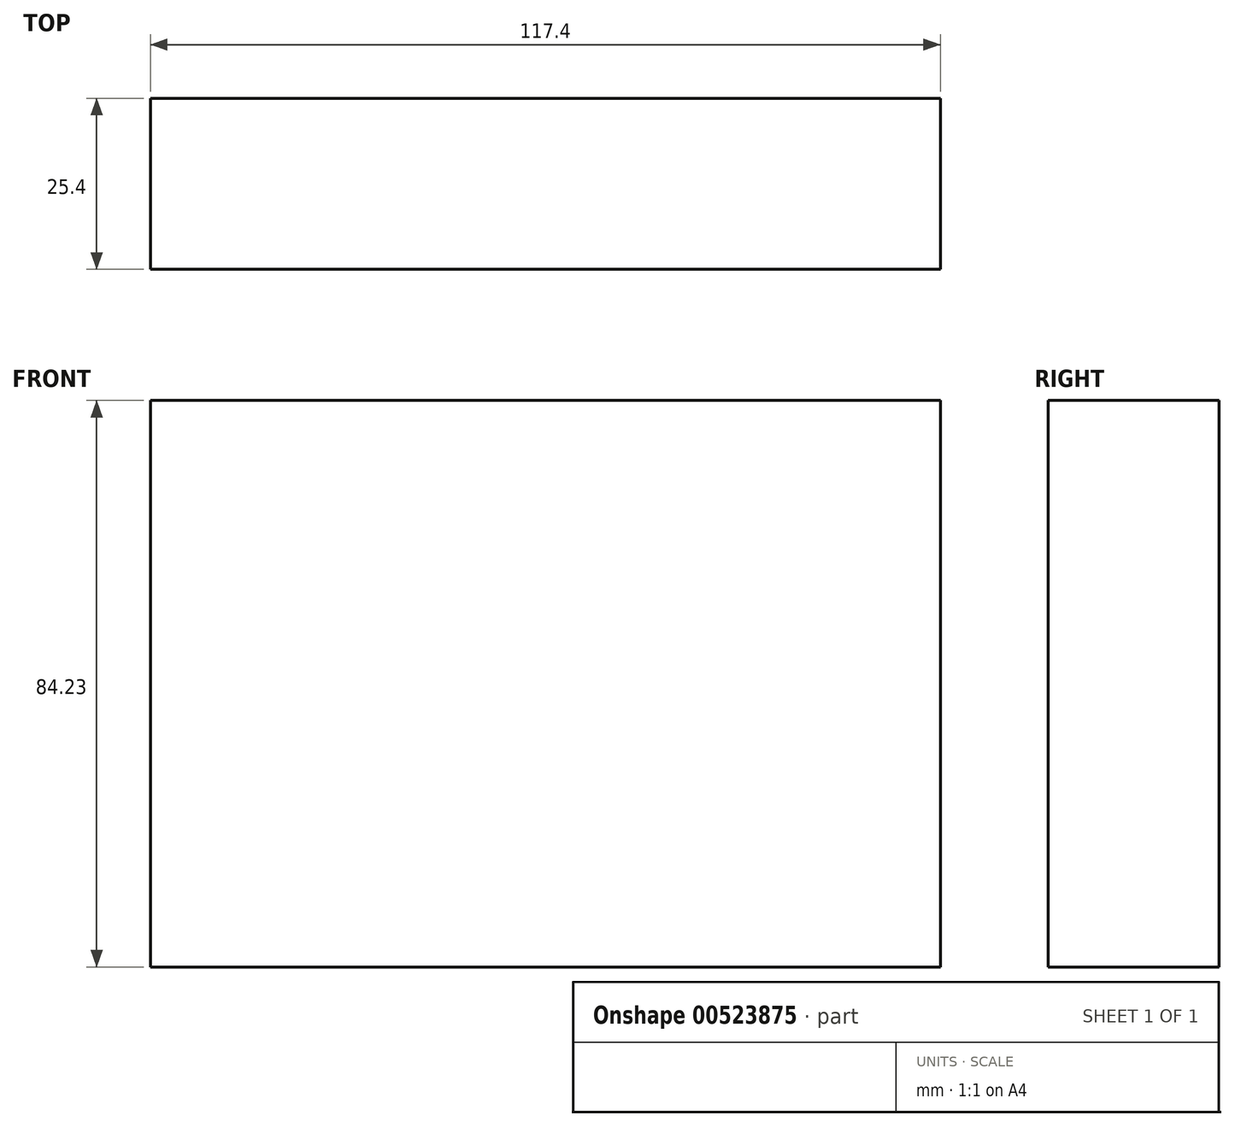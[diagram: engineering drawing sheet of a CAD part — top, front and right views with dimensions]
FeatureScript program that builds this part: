
annotation { "Feature Type Name" : "Feature", "Feature Type Description" : "" }
export const myFeature = defineFeature(function(context is Context, id is Id, definition is map)
    precondition{}
    {
        {
            var Q0;
            Q0=qCreatedBy(makeId("Front.planeOp"),FACE);
            var sketch = newSketch(context, id + "F0", { "sketchPlane" : qUnion([Q0])});
            skLineSegment(sketch, "E0", {"start": v(-57.38, 47.65) * mm, "end": v(60.02, 47.65) * mm});
            skLineSegment(sketch, "E1", {"start": v(60.02, 47.65) * mm, "end": v(60.02, -36.58) * mm});
            skLineSegment(sketch, "E2", {"start": v(60.02, -36.58) * mm, "end": v(-57.38, -36.58) * mm});
            skLineSegment(sketch, "E3", {"start": v(-57.38, -36.58) * mm, "end": v(-57.38, 47.65) * mm});
            skSolve(sketch);
        }
        {
            var Q0;
            Q0 = qSketchRegion(id + "F0", true);
            extrude(context, id + "F1", {"entities" : qUnion([Q0]), "depth" : 25.4 * mm, "offsetDistance" : 25.4 * mm});
        }
    });
